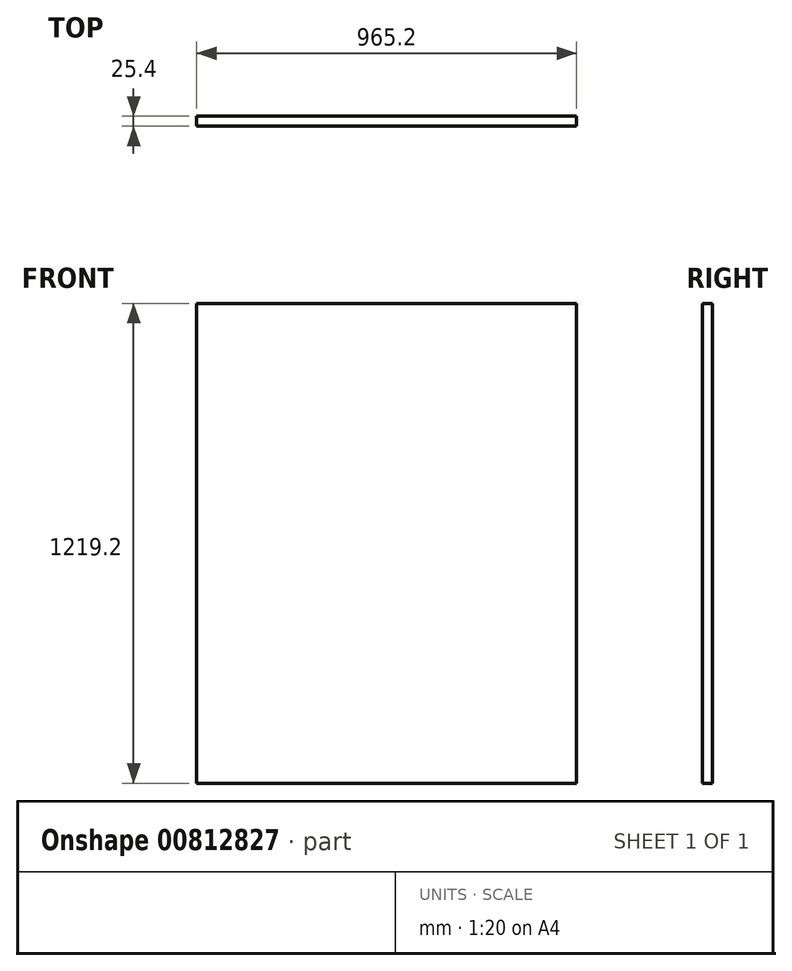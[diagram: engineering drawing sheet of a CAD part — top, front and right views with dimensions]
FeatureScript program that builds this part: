
annotation { "Feature Type Name" : "Feature", "Feature Type Description" : "" }
export const myFeature = defineFeature(function(context is Context, id is Id, definition is map)
    precondition{}
    {
        {
            var Q0;
            Q0=qCreatedBy(makeId("Front.planeOp"),FACE);
            var sketch = newSketch(context, id + "F0", { "sketchPlane" : qUnion([Q0])});
            skLineSegment(sketch, "E0.bottom", {"start": v(-482.6, 609.6) * mm, "end": v(482.6, 609.6) * mm});
            skLineSegment(sketch, "E0.top", {"start": v(-482.6, -609.6) * mm, "end": v(482.6, -609.6) * mm});
            skLineSegment(sketch, "E0.left", {"start": v(-482.6, 609.6) * mm, "end": v(-482.6, -609.6) * mm});
            skLineSegment(sketch, "E0.right", {"start": v(482.6, 609.6) * mm, "end": v(482.6, -609.6) * mm});
            skPoint(sketch, "E0.middle", {"position": v(0, 0) * mm});
            skSolve(sketch);
        }
        {
            var Q0;
            Q0 = qSketchRegion(id + "F0", true);
            extrude(context, id + "F1", {"entities" : qUnion([Q0]), "depth" : 25.4 * mm, "offsetDistance" : 25.4 * mm});
        }
    });
